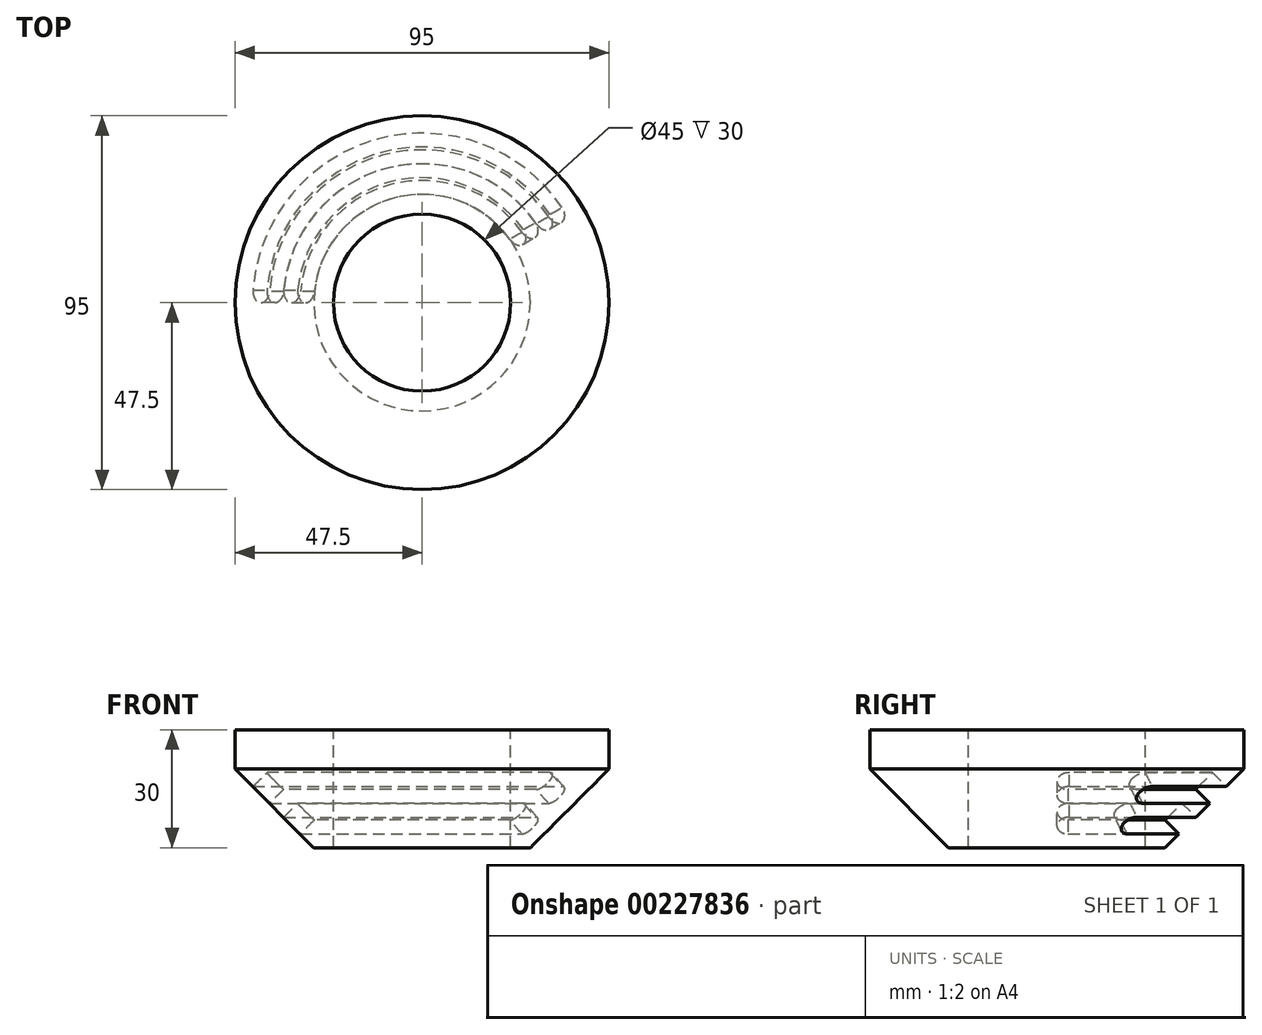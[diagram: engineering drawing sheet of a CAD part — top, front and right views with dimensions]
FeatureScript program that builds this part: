
annotation { "Feature Type Name" : "Feature", "Feature Type Description" : "" }
export const myFeature = defineFeature(function(context is Context, id is Id, definition is map)
    precondition{}
    {
        {
            var Q0;
            Q0=qCreatedBy(makeId("Front.planeOp"),FACE);
            var sketch = newSketch(context, id + "F0", { "sketchPlane" : qUnion([Q0])});
            skLineSegment(sketch, "E0", {"start": v(0, 70.12) * mm, "end": v(0, -51.14) * mm, "construction": true});
            skLineSegment(sketch, "E1", {"start": v(-11.66, 30) * mm, "end": v(-11.66, 0) * mm, "construction": true});
            skLineSegment(sketch, "E2", {"start": v(-22.5, 30) * mm, "end": v(-22.5, 0) * mm});
            skLineSegment(sketch, "E3", {"start": v(-27.5, 0) * mm, "end": v(-22.5, 0) * mm});
            skLineSegment(sketch, "E4", {"start": v(-27.5, 0) * mm, "end": v(-47.5, 20) * mm});
            skLineSegment(sketch, "E5", {"start": v(-50.84, 25) * mm, "end": v(-22.5, 25) * mm, "construction": true});
            skLineSegment(sketch, "E6", {"start": v(6.22, 30) * mm, "end": v(0, 30) * mm});
            skLineSegment(sketch, "E7.trimOffspring", {"start": v(-22.5, 30) * mm, "end": v(-50.84, 30) * mm});
            skLineSegment(sketch, "E8.trimOffspring", {"start": v(-11.66, 25) * mm, "end": v(18.2, 25) * mm, "construction": true});
            skPoint(sketch, "E9.end.orphan", {"position": v(-12.5, 0) * mm});
            skCircle(sketch, "E10", {"center": v(-27.5, 0) * mm, "radius": 5 * mm, "construction": true});
            skCircle(sketch, "E11", {"center": v(-27.5, 0) * mm, "radius": 8 * mm, "construction": true});
            skCircle(sketch, "E12", {"center": v(-27.5, 0) * mm, "radius": 11 * mm, "construction": true});
            skCircle(sketch, "E13", {"center": v(-27.5, 0) * mm, "radius": 16 * mm, "construction": true});
            skCircle(sketch, "E14", {"center": v(-27.5, 0) * mm, "radius": 19 * mm, "construction": true});
            skCircle(sketch, "E15", {"center": v(-31.63, -6.85) * mm, "radius": 3 * mm, "construction": true});
            skCircle(sketch, "E16", {"center": v(-38.6, -15.42) * mm, "radius": 3 * mm, "construction": true});
            skCircle(sketch, "E17", {"center": v(-27.5, 0) * mm, "radius": 22 * mm, "construction": true});
            skCircle(sketch, "E18", {"center": v(-27.5, 0) * mm, "radius": 25 * mm, "construction": true});
            skLineSegment(sketch, "E19", {"start": v(-47.5, 20) * mm, "end": v(-47.5, 41.36) * mm});
            skSolve(sketch);
        }
        {
            var Q0;
            Q0=makeQuery(id+"F0.imprint","IMPRINT",FACE,{"disambiguationData":[TD([[makeQuery(id+"F0.imprint","IMPRINT",EDGE,{"derivedFrom":sQuery(id+"F0.wireOp",EDGE,"E2")}),-1.0]])]});
            var Q1;
            Q1=sQuery(id+"F0.wireOp",EDGE,"E0");
            revolve(context, id + "F1", {"entities" : qUnion([Q0]), "axis" : qUnion([Q1]), "revolveType" : RevolveType.FULL});
        }
        {
            var Q0;
            Q0=qCreatedBy(makeId("Front.planeOp"),FACE);
            var sketch = newSketch(context, id + "F2", { "sketchPlane" : qUnion([Q0])});
            skLineSegment(sketch, "E20", {"start": v(0, 44.43) * mm, "end": v(0, -17.91) * mm, "construction": true});
            skCircle(sketch, "E21.0", {"center": v(-27.5, 0) * mm, "radius": 8 * mm, "construction": true});
            skCircle(sketch, "E22.0", {"center": v(-27.5, 0) * mm, "radius": 19 * mm, "construction": true});
            skLineSegment(sketch, "E23", {"start": v(-39.52, 19.1) * mm, "end": v(-35.28, 14.85) * mm});
            skCircle(sketch, "E24.0", {"center": v(-27.5, 0) * mm, "radius": 11 * mm, "construction": true});
            skCircle(sketch, "E24.1", {"center": v(-27.5, 0) * mm, "radius": 5 * mm, "construction": true});
            skCircle(sketch, "E25.0", {"center": v(-27.5, 0) * mm, "radius": 22 * mm, "construction": true});
            skCircle(sketch, "E25.1", {"center": v(-27.5, 0) * mm, "radius": 16 * mm, "construction": true});
            skLineSegment(sketch, "E26", {"start": v(-45.18, 13.44) * mm, "end": v(-39.52, 19.1) * mm});
            skLineSegment(sketch, "E27", {"start": v(-40.94, 9.2) * mm, "end": v(-35.28, 14.85) * mm});
            skLineSegment(sketch, "E28", {"start": v(-37.4, 5.66) * mm, "end": v(-31.74, 11.31) * mm});
            skLineSegment(sketch, "E29", {"start": v(-33.16, 1.41) * mm, "end": v(-27.5, 7.07) * mm});
            skLineSegment(sketch, "E30.trimOffspring", {"start": v(-31.74, 11.31) * mm, "end": v(-27.5, 7.07) * mm});
            skPoint(sketch, "E31.orphan", {"position": v(-47.5, 20) * mm});
            skLineSegment(sketch, "E32.trimOffspring", {"start": v(-40.94, 9.2) * mm, "end": v(-45.18, 13.44) * mm});
            skLineSegment(sketch, "E33.trimOffspring", {"start": v(-33.16, 1.41) * mm, "end": v(-37.4, 5.66) * mm});
            skSolve(sketch);
        }
        {
            var Q0;
            Q0=qSketchRegion(id+"F2",true);
            var Q1;
            Q1=sQuery(id+"F2.wireOp",EDGE,"E20");
            revolve(context, id + "F3", {"entities" : qUnion([Q0]), "axis" : qUnion([Q1]), "revolveType" : RevolveType.ONE_DIRECTION, "angle" : 150 * degree});
        }
        {
            var Q0;
            Q0=makeQuery(id+"F3.opRevolve","CAP_EDGE",EDGE,{"disambiguationData":[OSD([sQuery(id+"F2.wireOp",EDGE,"E26")])],"isStart":true});
            var Q1;
            Q1=makeQuery(id+"F3.opRevolve","CAP_EDGE",EDGE,{"disambiguationData":[OSD([sQuery(id+"F2.wireOp",EDGE,"E27")])],"isStart":true});
            var Q2;
            Q2=makeQuery(id+"F3.opRevolve","CAP_EDGE",EDGE,{"disambiguationData":[OSD([sQuery(id+"F2.wireOp",EDGE,"E29")])],"isStart":true});
            var Q3;
            Q3=makeQuery(id+"F3.opRevolve","CAP_EDGE",EDGE,{"disambiguationData":[OSD([sQuery(id+"F2.wireOp",EDGE,"E28")])],"isStart":true});
            var Q4;
            Q4=makeQuery(id+"F3.opRevolve","CAP_EDGE",EDGE,{"disambiguationData":[OSD([sQuery(id+"F2.wireOp",EDGE,"E29")])],"isStart":false});
            var Q5;
            Q5=makeQuery(id+"F3.opRevolve","CAP_EDGE",EDGE,{"disambiguationData":[OSD([sQuery(id+"F2.wireOp",EDGE,"E28")])],"isStart":false});
            var Q6;
            Q6=makeQuery(id+"F3.opRevolve","CAP_EDGE",EDGE,{"disambiguationData":[OSD([sQuery(id+"F2.wireOp",EDGE,"E27")])],"isStart":false});
            var Q7;
            Q7=makeQuery(id+"F3.opRevolve","CAP_EDGE",EDGE,{"disambiguationData":[OSD([sQuery(id+"F2.wireOp",EDGE,"E26")])],"isStart":false});
            fillet(context, id + "F4", {"entities" : qUnion([Q0, Q1, Q2, Q3, Q4, Q5, Q6, Q7]), "radius" : 3 * mm, "tangentPropagation" : true, "allowEdgeOverflow" : false});
        }
        {
            var Q0;
            Q0=makeQuery(id+"F3.opRevolve","SWEPT_BODY",BODY,{"disambiguationData":[OSD([sQuery(id+"F2.wireOp",EDGE,"E28"),sQuery(id+"F2.wireOp",EDGE,"E29"),sQuery(id+"F2.wireOp",EDGE,"E30.trimOffspring"),sQuery(id+"F2.wireOp",EDGE,"E33.trimOffspring")])]});
            var Q1;
            Q1=makeQuery(id+"F3.opRevolve","SWEPT_BODY",BODY,{"disambiguationData":[OSD([sQuery(id+"F2.wireOp",EDGE,"E23"),sQuery(id+"F2.wireOp",EDGE,"E26"),sQuery(id+"F2.wireOp",EDGE,"E27"),sQuery(id+"F2.wireOp",EDGE,"E32.trimOffspring")])]});
            var Q2;
            Q2=makeQuery(id+"F1.opRevolve","SWEPT_BODY",BODY,{"disambiguationData":[OSD([sQuery(id+"F0.wireOp",EDGE,"E2"),sQuery(id+"F0.wireOp",EDGE,"E3"),sQuery(id+"F0.wireOp",EDGE,"E4"),sQuery(id+"F0.wireOp",EDGE,"E7.trimOffspring"),sQuery(id+"F0.wireOp",EDGE,"E19")])]});
            booleanBodies(context, id + "F5", {"operationType" : BooleanOperationType.SUBTRACTION, "tools" : qUnion([Q0, Q1]), "targets" : qUnion([Q2])});
        }
    });
